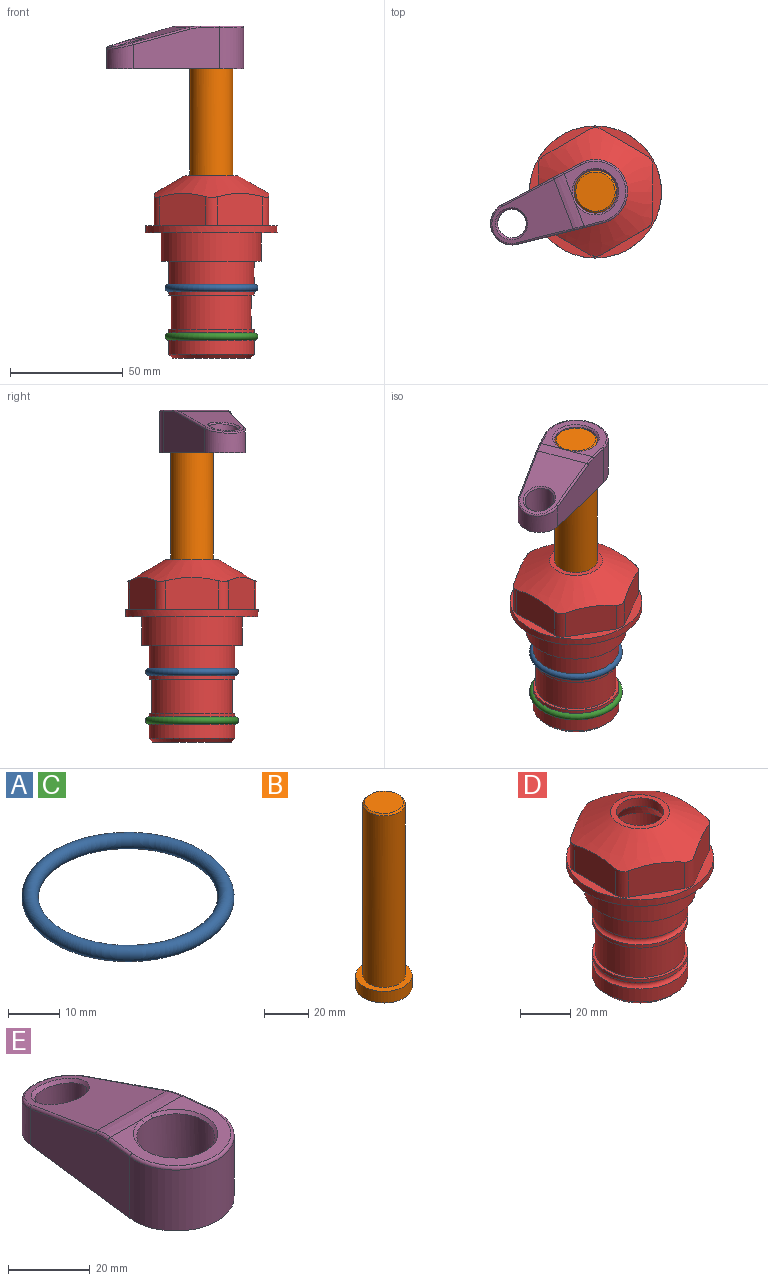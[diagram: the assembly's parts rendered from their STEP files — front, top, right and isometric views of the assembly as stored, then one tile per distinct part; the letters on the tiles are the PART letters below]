
ASSEMBLY  parts=5 mates=4
PART A: 1 faces, bbox 44.7x44.7x3.2 mm
  f0: torus R=19.05mm, axis (0,0,1), area 1193.9mm2
PART B: 6 faces, bbox 25.4x25.4x101.6 mm
  f0: plane 17.46x17.46mm, normal (0,0,1), area 239.5mm2, adj f5
  f1: plane 25.4x25.4mm, normal (0,0,-1), area 506.7mm2, adj f2
  f2: cylinder r=12.7mm len=25.4mm, axis (0,0,1), area 506.7mm2, adj f1,f3
  f3: plane 25.4x25.4mm, normal (0,0,1), area 221.7mm2, adj f2,f4
  f4: cylinder r=9.53mm len=94.46mm, axis (0,0,1), area 5653mm2, adj f3,f5
  f5: cone r=8.73mm half-angle=45deg, axis (0,0,-1), area 64.4mm2, adj f0,f4
PART C: same geometry as A
PART D: 36 faces, bbox 58.7x58.7x81 mm
  f0: cylinder r=17.78mm len=35.56mm, axis (0,0,1), area 1670.8mm2, adj f23,f24,f31
  f1: cylinder r=19.05mm len=38.1mm, axis (0,0,1), area 1191.9mm2, adj f26,f27,f30
  f2: plane 58.66x58.66mm, normal (0,0,-1), area 1150.6mm2, adj f3,f28
  f3: cylinder r=29.33mm len=58.66mm, axis (0,0,-1), area 585.1mm2, adj f2,f4
  f4: plane 58.66x58.66mm, normal (0,0,1), area 475.9mm2, adj f3,f5,f6,f7,f8,f9,f10,f11
  f5: plane 20.32x14.34mm, normal (-0.5,0.87,0), area 324.4mm2, adj f4,f15,f16,f17
  f6: plane 20.32x14.34mm, normal (0.5,0.87,0), area 324.4mm2, adj f4,f14,f15,f17
  f7: plane 23.48x14.34mm, normal (1,0,0), area 324.4mm2, adj f4,f13,f14,f17
  f8: plane 20.32x14.34mm, normal (0.5,-0.87,0), area 324.4mm2, adj f4,f12,f13,f17
  f9: plane 20.32x14.34mm, normal (-0.5,-0.87,0), area 324.4mm2, adj f4,f11,f12,f17
  f10: plane 23.48x14.34mm, normal (-1,0,0), area 324.4mm2, adj f4,f11,f16,f17
  f11: cylinder r=5.08mm len=12.85mm, axis (0,0,-1), area 67.2mm2, adj f4,f9,f10,f17
  f12: cylinder r=5.08mm len=12.85mm, axis (0,0,-1), area 67.2mm2, adj f4,f8,f9,f17
  f13: cylinder r=5.08mm len=12.85mm, axis (0,0,-1), area 67.2mm2, adj f4,f7,f8,f17
  f14: cylinder r=5.08mm len=12.85mm, axis (0,0,-1), area 67.2mm2, adj f4,f6,f7,f17
  f15: cylinder r=5.08mm len=12.85mm, axis (0,0,-1), area 67.2mm2, adj f4,f5,f6,f17
  f16: cylinder r=5.08mm len=12.85mm, axis (0,0,-1), area 67.2mm2, adj f4,f5,f10,f17
  f17: cone r=11.73mm half-angle=60deg, axis (0,0,-1), area 2071.8mm2, adj f5,f6,f7,f8,f9,f10,f11,f12
  f18: plane 23.46x23.46mm, normal (0,0,1), area 147.4mm2, adj f17,f35
  f19: plane 34.93x34.93mm, normal (0,0,-1), area 958mm2, adj f29
  f20: cylinder r=19.05mm len=38.1mm, axis (0,0,1), area 760.1mm2, adj f21,f29
  f21: torus R=19.05mm, axis (0,0,1), area 565.3mm2, adj f20,f22
  f22: cylinder r=19.05mm len=38.1mm, axis (0,0,1), area 190mm2, adj f21,f23
  f23: plane 38.1x38.1mm, normal (0,0,1), area 146.9mm2, adj f0,f22
  f24: plane 38.1x38.1mm, normal (0,0,-1), area 146.9mm2, adj f0,f25
  f25: cylinder r=19.05mm len=38.1mm, axis (0,0,1), area 190mm2, adj f24,f26
  f26: torus R=19.05mm, axis (0,0,1), area 565.3mm2, adj f1,f25
  f27: plane 44.45x44.45mm, normal (0,0,-1), area 411.7mm2, adj f1,f28
  f28: cylinder r=22.23mm len=44.45mm, axis (0,0,1), area 1773.5mm2, adj f2,f27
  f29: cone r=19.05mm half-angle=45deg, axis (0,0,1), area 257.5mm2, adj f19,f20
  f30: cylinder r=3.17mm len=6.75mm, axis (-1,0,0), area 128mm2, adj f1,f33
  f31: cylinder r=3.17mm len=6.35mm, axis (-1,0,0), area 102.5mm2, adj f0,f33
  f32: plane 25.4x25.4mm, normal (0,0,1), area 506.7mm2, adj f33
  f33: cylinder r=12.7mm len=66.42mm, axis (0,0,-1), area 5236.2mm2, adj f30,f31,f32,f34
  f34: cone r=9.53mm half-angle=30deg, axis (0,0,-1), area 443.4mm2, adj f33,f35
  f35: cylinder r=9.53mm len=19.05mm, axis (0,0,-1), area 240.9mm2, adj f18,f34
PART E: 31 faces, bbox 31.7x65.5x19.8 mm
  f0: plane 39.12x18.26mm, normal (0.99,0.12,0), area 612.2mm2, adj f1,f4,f7,f11,f13,f15
  f1: cylinder r=9.53mm len=18.91mm, axis (0,0,-1), area 296.1mm2, adj f0,f2,f7,f17
  f2: plane 39.12x18.26mm, normal (-0.99,0.12,0), area 612.2mm2, adj f1,f4,f7,f12,f14,f16
  f3: cylinder r=6.35mm len=12.7mm, axis (0,0,-1), area 362.4mm2, adj f7,f18
  f4: cylinder r=14.29mm len=28.58mm, axis (0,0,-1), area 882.2mm2, adj f0,f2,f7,f10
  f5: cylinder r=9.53mm len=19.05mm, axis (0,0,-1), area 1092.6mm2, adj f7,f19,f20
  f6: plane 26.99x23.69mm, normal (0,0,1), area 216.2mm2, adj f9,f10,f11,f12,f19
  f7: plane 63.5x28.58mm, normal (0,0,-1), area 661.8mm2, adj f0,f1,f2,f3,f4,f5,f22,f23
  f8: plane 33.52x23.6mm, normal (0,0.26,0.97), area 486mm2, adj f9,f15,f16,f17,f18
  f9: cylinder r=19.05mm len=24.72mm, axis (1,0,0), area 120.4mm2, adj f6,f8,f13,f14,f20
  f10: torus R=13.49mm, axis (0,0,1), area 59mm2, adj f4,f6,f11,f12
  f11: cylinder r=0.79mm len=8.67mm, axis (0.12,-0.99,0), area 10.8mm2, adj f0,f6,f10,f13
  f12: cylinder r=0.79mm len=8.67mm, axis (0.12,0.99,0), area 10.8mm2, adj f2,f6,f10,f14
  f13: bspline ~4.95x1.42mm, area 6.1mm2, adj f0,f9,f11,f15
  f14: bspline ~4.95x1.42mm, area 6.1mm2, adj f2,f9,f12,f16
  f15: cylinder r=0.79mm len=25.95mm, axis (0.12,-0.96,0.26), area 32.9mm2, adj f0,f8,f13,f17
  f16: cylinder r=0.79mm len=25.95mm, axis (0.12,0.96,-0.26), area 32.9mm2, adj f2,f8,f14,f17
  f17: bspline ~18.91x8.38mm, area 30mm2, adj f1,f8,f15,f16
  f18: bspline ~14.29x14.29mm, area 48.3mm2, adj f3,f8
  f19: cone r=9.53mm half-angle=45deg, axis (0,0,1), area 66.5mm2, adj f5,f6,f20
  f20: bspline ~3.22x0.96mm, area 3.5mm2, adj f5,f9,f19
  f21: plane 2.75x2.72mm, normal (0,0,-1), area 2.9mm2, adj f23,f25,f28
  f22: plane 23.05x15.88mm, normal (-0.99,-0.12,0), area 323.6mm2, adj f7,f25,f26,f27,f28,f29
  f23: plane 23.05x15.88mm, normal (0.99,-0.12,0), area 323.6mm2, adj f7,f21,f25,f27,f28,f30
  f24: cylinder r=9.53mm len=10.69mm, axis (0,0,-1), area 114.7mm2, adj f7,f27,f29,f30
  f25: cylinder r=12.7mm len=20.59mm, axis (0,0,-1), area 381.1mm2, adj f7,f21,f22,f23,f26,f28
  f26: plane 2.75x2.72mm, normal (0,0,-1), area 2.9mm2, adj f22,f25,f28
  f27: plane 19.72x18.37mm, normal (0,-0.26,-0.97), area 291.8mm2, adj f22,f23,f24,f28,f29,f30
  f28: cylinder r=15.88mm len=19.92mm, axis (1,0,0), area 54.8mm2, adj f21,f22,f23,f25,f26,f27
  f29: cylinder r=1.59mm len=11mm, axis (0,0,-1), area 34.7mm2, adj f7,f22,f24,f27
  f30: cylinder r=1.59mm len=11mm, axis (0,0,-1), area 34.7mm2, adj f7,f23,f24,f27
PLACE A t=(1.88,-4.43,2.65)mm
PLACE B rot(axis=(0,0,1),110.9deg) t=(1.88,-4.43,30.2)mm
PLACE C t=(1.88,-4.43,-18.94)mm
PLACE D t=(1.88,-4.43,2.65)mm fixed
PLACE E rot(axis=(0,0,1),110.9deg) t=(1.88,-4.43,30.99)mm
MATE fastened B.f2 <-> E.f4  axis (0,0,1) through (1.88,-4.43,93.7)mm
MATE fastened D.f0 <-> C.f0  axis (0,0,1) through (1.88,-4.43,-43.45)mm
MATE fastened D.f0 <-> A.f0  axis (0,0,1) through (1.88,-4.43,-21.86)mm
MATE cylindrical B.f2 <-> D.f0  axis (0,0,-1) through (1.88,-4.43,-7.9)mm
